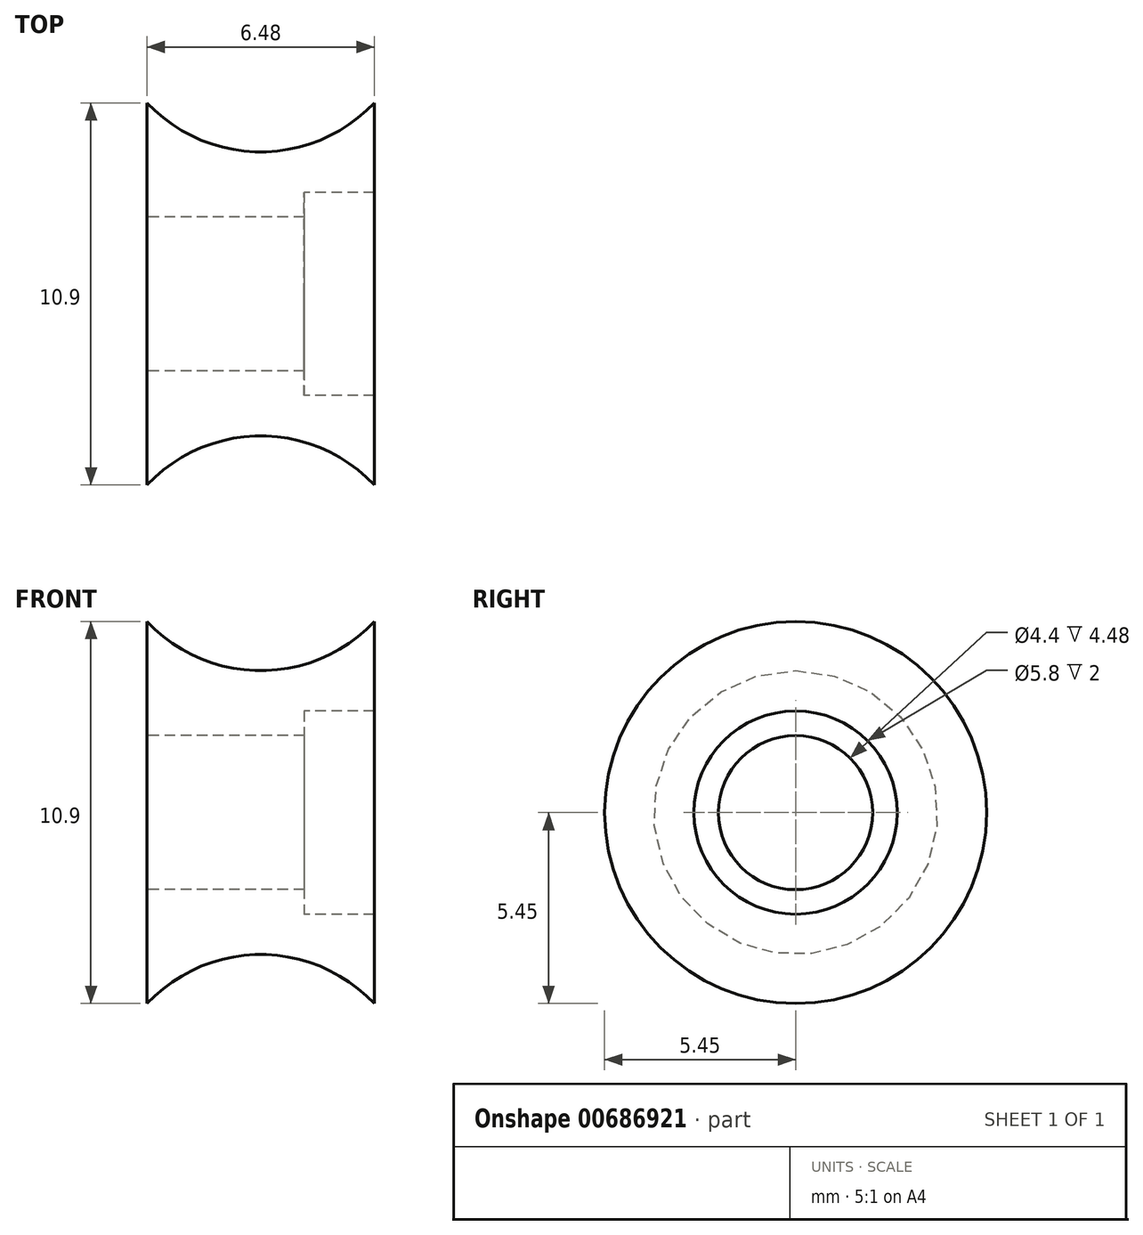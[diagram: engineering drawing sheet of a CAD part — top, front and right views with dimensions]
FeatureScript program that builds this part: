
annotation { "Feature Type Name" : "Feature", "Feature Type Description" : "" }
export const myFeature = defineFeature(function(context is Context, id is Id, definition is map)
    precondition{}
    {
        {
            var Q0;
            Q0=qCreatedBy(makeId("Front.planeOp"),FACE);
            var sketch = newSketch(context, id + "F0", { "sketchPlane" : qUnion([Q0])});
            skLineSegment(sketch, "E0", {"start": v(-15.22, 0) * mm, "end": v(15.18, 0) * mm, "construction": true});
            skLineSegment(sketch, "E1", {"start": v(-4.48, 2.2) * mm, "end": v(0, 2.2) * mm});
            skLineSegment(sketch, "E2", {"start": v(0, 2.2) * mm, "end": v(0, 2.9) * mm});
            skLineSegment(sketch, "E3", {"start": v(0, 2.9) * mm, "end": v(2, 2.9) * mm});
            skLineSegment(sketch, "E4", {"start": v(2, 2.9) * mm, "end": v(2, 5.45) * mm});
            skLineSegment(sketch, "E5", {"start": v(-4.48, 5.45) * mm, "end": v(-4.48, 2.2) * mm});
            skArc(sketch, "E6", {"start": v(-4.48, 5.45) * mm, "mid": v(-1.24, 4.05) * mm, "end": v(2, 5.45) * mm});
            skSolve(sketch);
        }
        {
            var Q0;
            Q0 = qSketchRegion(id + "F0", true);
            var Q1;
            Q1=sQuery(id+"F0.wireOp",EDGE,"E0");
            revolve(context, id + "F1", {"entities" : qUnion([Q0]), "axis" : qUnion([Q1]), "revolveType" : RevolveType.FULL});
        }
    });
